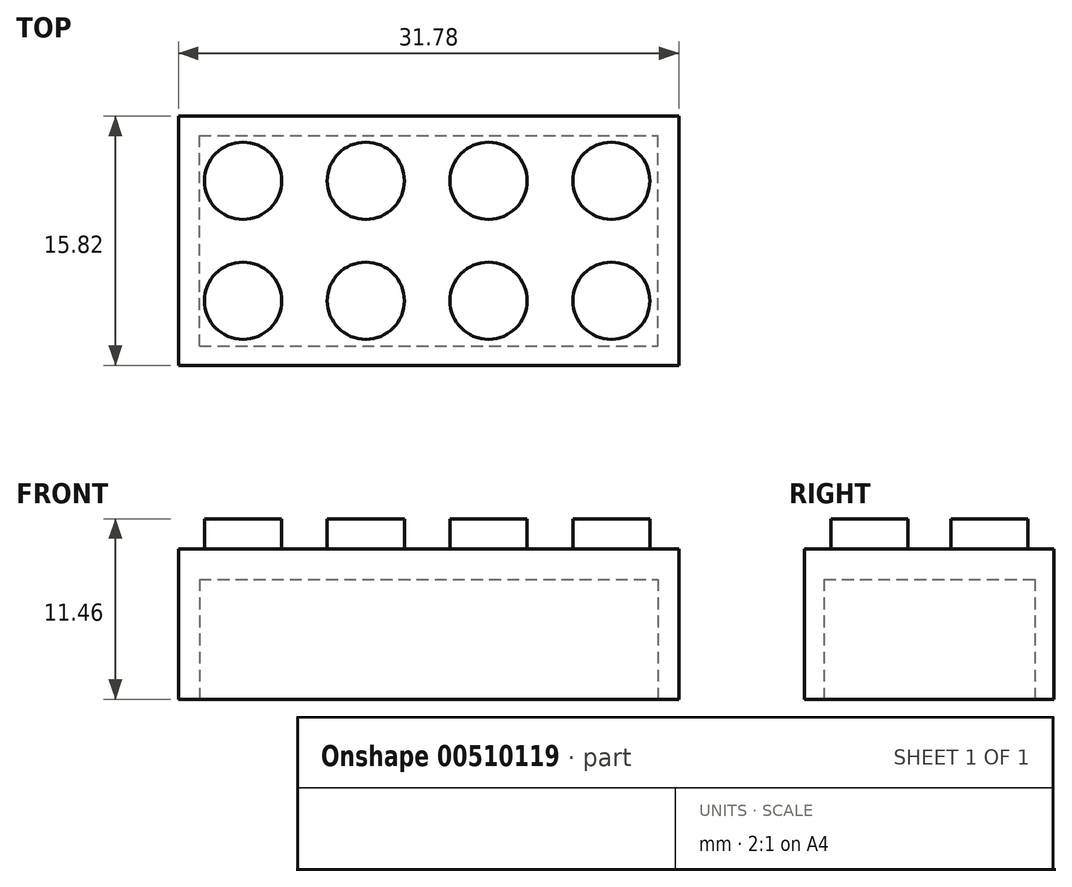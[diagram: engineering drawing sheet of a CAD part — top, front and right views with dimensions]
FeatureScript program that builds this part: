
annotation { "Feature Type Name" : "Feature", "Feature Type Description" : "" }
export const myFeature = defineFeature(function(context is Context, id is Id, definition is map)
    precondition{}
    {
        {
            var Q0;
            Q0=qCreatedBy(makeId("Top.planeOp"),FACE);
            var sketch = newSketch(context, id + "F0", { "sketchPlane" : qUnion([Q0])});
            skLineSegment(sketch, "E0.bottom", {"start": v(15.89, -7.91) * mm, "end": v(-15.89, -7.91) * mm});
            skLineSegment(sketch, "E0.top", {"start": v(15.89, 7.91) * mm, "end": v(-15.89, 7.91) * mm});
            skLineSegment(sketch, "E0.left", {"start": v(15.89, -7.91) * mm, "end": v(15.89, 7.91) * mm});
            skLineSegment(sketch, "E0.right", {"start": v(-15.89, -7.91) * mm, "end": v(-15.89, 7.91) * mm});
            skPoint(sketch, "E0.middle", {"position": v(0, 0) * mm});
            skSolve(sketch);
        }
        {
            var Q0;
            Q0 = qSketchRegion(id + "F0", true);
            extrude(context, id + "F1", {"entities" : qUnion([Q0]), "depth" : 9.55 * mm, "offsetDistance" : 25.4 * mm});
        }
        {
            var Q0;
            Q0=makeQuery(id+"F1.opExtrude","CAP_FACE",FACE,{"disambiguationData":[OSD([sQuery(id+"F0.wireOp",EDGE,"E0.bottom"),sQuery(id+"F0.wireOp",EDGE,"E0.top"),sQuery(id+"F0.wireOp",EDGE,"E0.left"),sQuery(id+"F0.wireOp",EDGE,"E0.right")])],"isStart":false});
            var sketch = newSketch(context, id + "F2", { "sketchPlane" : qUnion([Q0])});
            skCircle(sketch, "E1", {"center": v(-11.79, 3.8) * mm, "radius": 2.45 * mm});
            skSolve(sketch);
        }
        {
            var Q0;
            Q0=makeQuery(id+"F2.imprint","IMPRINT",FACE,{"disambiguationData":[TD([[makeQuery(id+"F2.imprint","IMPRINT",EDGE,{"derivedFrom":sQuery(id+"F2.wireOp",EDGE,"E1")}),-1.0]])]});
            var sketch = newSketch(context, id + "F3", { "sketchPlane" : qUnion([Q0])});
            skCircle(sketch, "E2", {"center": v(-11.79, -3.81) * mm, "radius": 2.45 * mm});
            skSolve(sketch);
        }
        {
            var Q0;
            Q0 = qSketchRegion(id + "F2", true);
            extrude(context, id + "F4", {"entities" : qUnion([Q0]), "operationType" : NewBodyOperationType.ADD, "depth" : 1.9 * mm, "offsetDistance" : 25.4 * mm});
        }
        {
            var Q0;
            Q0 = qSketchRegion(id + "F3", true);
            extrude(context, id + "F5", {"entities" : qUnion([Q0]), "operationType" : NewBodyOperationType.ADD, "depth" : 1.9 * mm, "offsetDistance" : 25.4 * mm});
        }
        {
            var Q0;
            Q0=makeQuery(id+"F1.opExtrude","CAP_FACE",FACE,{"disambiguationData":[OSD([sQuery(id+"F0.wireOp",EDGE,"E0.bottom"),sQuery(id+"F0.wireOp",EDGE,"E0.top"),sQuery(id+"F0.wireOp",EDGE,"E0.left"),sQuery(id+"F0.wireOp",EDGE,"E0.right")])],"isStart":false});
            var sketch = newSketch(context, id + "F6", { "sketchPlane" : qUnion([Q0])});
            skCircle(sketch, "E3", {"center": v(-3.99, 3.81) * mm, "radius": 2.45 * mm});
            skSolve(sketch);
        }
        {
            var Q0;
            Q0=makeQuery(id+"F6.imprint","IMPRINT",FACE,{"disambiguationData":[TD([[makeQuery(id+"F6.imprint","IMPRINT",EDGE,{"derivedFrom":sQuery(id+"F6.wireOp",EDGE,"E3")}),-1.0]])]});
            var sketch = newSketch(context, id + "F7", { "sketchPlane" : qUnion([Q0])});
            skCircle(sketch, "E4", {"center": v(-3.99, -3.8) * mm, "radius": 2.45 * mm});
            skSolve(sketch);
        }
        {
            var Q0;
            Q0 = qSketchRegion(id + "F6", true);
            extrude(context, id + "F8", {"entities" : qUnion([Q0]), "operationType" : NewBodyOperationType.ADD, "depth" : 1.9 * mm, "offsetDistance" : 25.4 * mm});
        }
        {
            var Q0;
            Q0 = qSketchRegion(id + "F7", true);
            extrude(context, id + "F9", {"entities" : qUnion([Q0]), "operationType" : NewBodyOperationType.ADD, "depth" : 1.9 * mm, "offsetDistance" : 25.4 * mm});
        }
        {
            var Q0;
            Q0=makeQuery(id+"F1.opExtrude","CAP_FACE",FACE,{"disambiguationData":[OSD([sQuery(id+"F0.wireOp",EDGE,"E0.bottom"),sQuery(id+"F0.wireOp",EDGE,"E0.top"),sQuery(id+"F0.wireOp",EDGE,"E0.left"),sQuery(id+"F0.wireOp",EDGE,"E0.right")])],"isStart":false});
            var sketch = newSketch(context, id + "F10", { "sketchPlane" : qUnion([Q0])});
            skCircle(sketch, "E5", {"center": v(3.81, 3.81) * mm, "radius": 2.45 * mm});
            skCircle(sketch, "E6", {"center": v(3.81, -3.8) * mm, "radius": 2.45 * mm});
            skSolve(sketch);
        }
        {
            var Q0;
            Q0 = qSketchRegion(id + "F10", true);
            extrude(context, id + "F11", {"entities" : qUnion([Q0]), "operationType" : NewBodyOperationType.ADD, "depth" : 1.9 * mm, "offsetDistance" : 25.4 * mm});
        }
        {
            var Q0;
            Q0=makeQuery(id+"F1.opExtrude","CAP_FACE",FACE,{"disambiguationData":[OSD([sQuery(id+"F0.wireOp",EDGE,"E0.bottom"),sQuery(id+"F0.wireOp",EDGE,"E0.top"),sQuery(id+"F0.wireOp",EDGE,"E0.left"),sQuery(id+"F0.wireOp",EDGE,"E0.right")])],"isStart":false});
            var sketch = newSketch(context, id + "F12", { "sketchPlane" : qUnion([Q0])});
            skCircle(sketch, "E7", {"center": v(11.6, 3.81) * mm, "radius": 2.45 * mm});
            skCircle(sketch, "E8", {"center": v(11.6, -3.8) * mm, "radius": 2.45 * mm});
            skSolve(sketch);
        }
        {
            var Q0;
            Q0 = qSketchRegion(id + "F12", true);
            extrude(context, id + "F13", {"entities" : qUnion([Q0]), "operationType" : NewBodyOperationType.ADD, "depth" : 1.9 * mm, "offsetDistance" : 25.4 * mm});
        }
        {
            var Q0;
            Q0=makeQuery(id+"F1.opExtrude","CAP_FACE",FACE,{"disambiguationData":[OSD([sQuery(id+"F0.wireOp",EDGE,"E0.bottom"),sQuery(id+"F0.wireOp",EDGE,"E0.top"),sQuery(id+"F0.wireOp",EDGE,"E0.left"),sQuery(id+"F0.wireOp",EDGE,"E0.right")])],"isStart":true});
            var sketch = newSketch(context, id + "F14", { "sketchPlane" : qUnion([Q0])});
            skLineSegment(sketch, "E9.bottom", {"start": v(-14.55, 6.7) * mm, "end": v(14.55, 6.7) * mm});
            skLineSegment(sketch, "E9.top", {"start": v(-14.55, -6.7) * mm, "end": v(14.55, -6.7) * mm});
            skLineSegment(sketch, "E9.left", {"start": v(-14.55, 6.7) * mm, "end": v(-14.55, -6.7) * mm});
            skLineSegment(sketch, "E9.right", {"start": v(14.55, 6.7) * mm, "end": v(14.55, -6.7) * mm});
            skPoint(sketch, "E9.middle", {"position": v(0, 0) * mm});
            skSolve(sketch);
        }
        {
            var Q0;
            Q0 = qSketchRegion(id + "F14", true);
            extrude(context, id + "F15", {"entities" : qUnion([Q0]), "operationType" : NewBodyOperationType.REMOVE, "oppositeDirection" : true, "depth" : 7.62 * mm, "offsetDistance" : 25.4 * mm});
        }
    });
